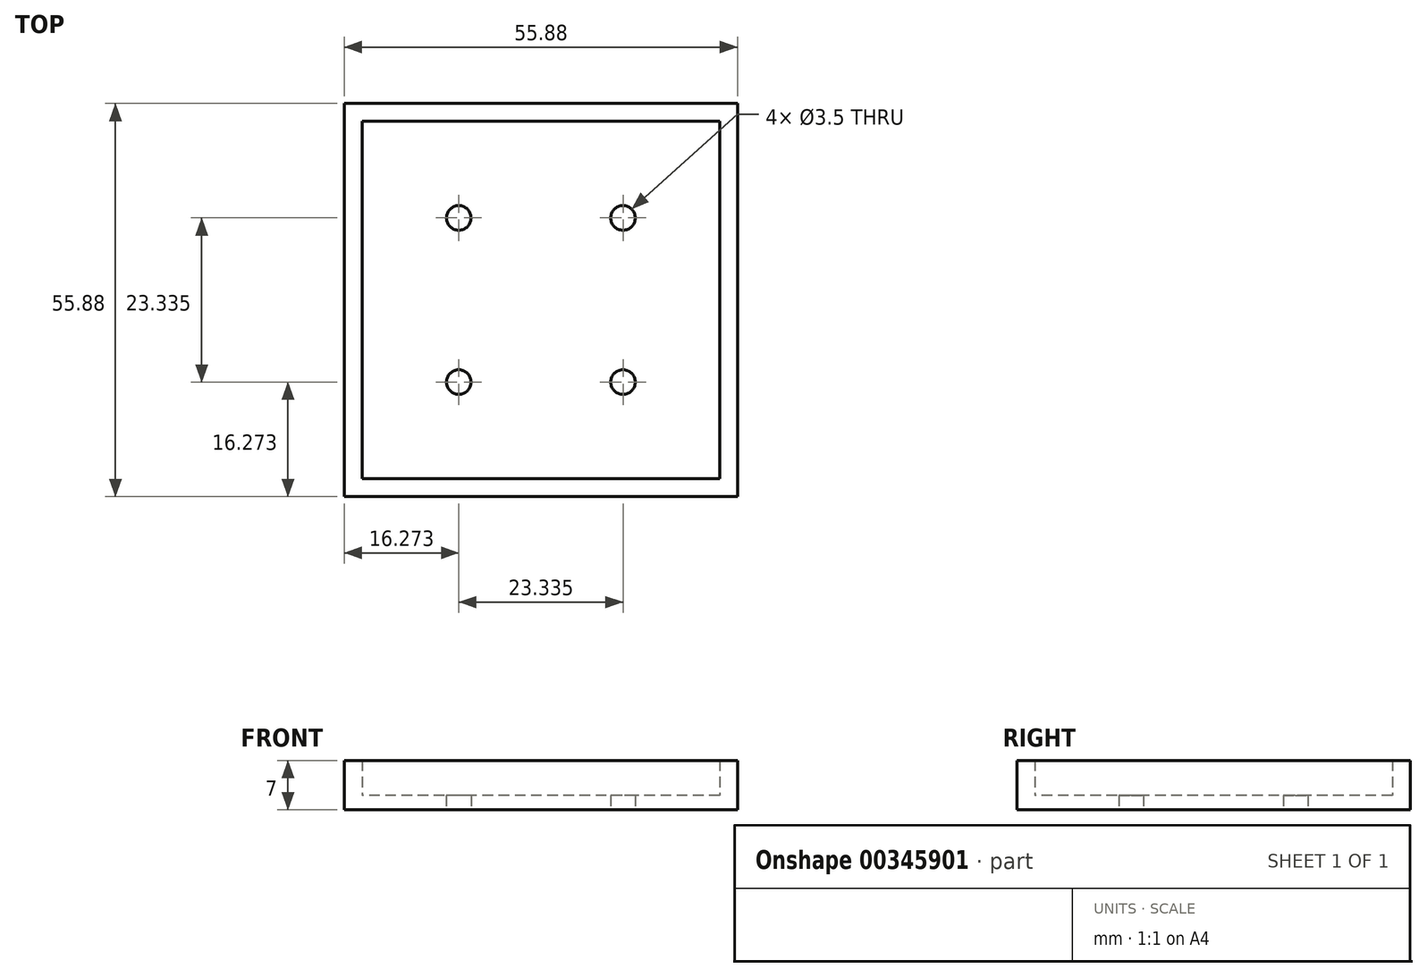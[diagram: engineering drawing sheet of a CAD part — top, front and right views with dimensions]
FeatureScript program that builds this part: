
annotation { "Feature Type Name" : "Feature", "Feature Type Description" : "" }
export const myFeature = defineFeature(function(context is Context, id is Id, definition is map)
    precondition{}
    {
        {
            var Q0;
            Q0=qCreatedBy(makeId("Top.planeOp"),FACE);
            var sketch = newSketch(context, id + "F0", { "sketchPlane" : qUnion([Q0])});
            skCircle(sketch, "E0", {"center": v(0, 0) * mm, "radius": 16.5 * mm, "construction": true});
            skCircle(sketch, "E1", {"center": v(-11.67, -11.67) * mm, "radius": 1.75 * mm});
            skCircle(sketch, "E2", {"center": v(-11.67, 11.67) * mm, "radius": 1.75 * mm});
            skCircle(sketch, "E3", {"center": v(11.67, 11.67) * mm, "radius": 1.75 * mm});
            skCircle(sketch, "E4", {"center": v(11.67, -11.67) * mm, "radius": 1.75 * mm});
            skLineSegment(sketch, "E5", {"start": v(-11.67, -11.67) * mm, "end": v(11.67, 11.67) * mm, "construction": true});
            skLineSegment(sketch, "E6", {"start": v(-11.67, 11.67) * mm, "end": v(11.67, -11.67) * mm, "construction": true});
            skLineSegment(sketch, "E7", {"start": v(-16.5, 0) * mm, "end": v(16.5, 0) * mm, "construction": true});
            skLineSegment(sketch, "E8.bottom", {"start": v(-27.94, 27.94) * mm, "end": v(27.94, 27.94) * mm});
            skLineSegment(sketch, "E8.top", {"start": v(-27.94, -27.94) * mm, "end": v(27.94, -27.94) * mm});
            skLineSegment(sketch, "E8.left", {"start": v(-27.94, 27.94) * mm, "end": v(-27.94, -27.94) * mm});
            skLineSegment(sketch, "E8.right", {"start": v(27.94, 27.94) * mm, "end": v(27.94, -27.94) * mm});
            skLineSegment(sketch, "E9", {"start": v(-27.94, -27.94) * mm, "end": v(27.94, 27.94) * mm, "construction": true});
            skSolve(sketch);
        }
        {
            var Q0;
            Q0=makeQuery(id+"F0.imprint","IMPRINT",FACE,{"disambiguationData":[TD([[makeQuery(id+"F0.imprint","IMPRINT",EDGE,{"derivedFrom":sQuery(id+"F0.wireOp",EDGE,"E1")}),-1.0]])]});
            extrude(context, id + "F1", {"entities" : qUnion([Q0]), "depth" : 2 * mm});
        }
        {
            var Q0;
            Q0=makeQuery(id+"F1.opExtrude","CAP_FACE",FACE,{"disambiguationData":[OSD([sQuery(id+"F0.wireOp",EDGE,"E1"),sQuery(id+"F0.wireOp",EDGE,"E2"),sQuery(id+"F0.wireOp",EDGE,"E3"),sQuery(id+"F0.wireOp",EDGE,"E4"),sQuery(id+"F0.wireOp",EDGE,"E8.bottom"),sQuery(id+"F0.wireOp",EDGE,"E8.top"),sQuery(id+"F0.wireOp",EDGE,"E8.left"),sQuery(id+"F0.wireOp",EDGE,"E8.right")])],"isStart":false});
            var sketch = newSketch(context, id + "F2", { "sketchPlane" : qUnion([Q0])});
            skLineSegment(sketch, "E10.bottom", {"start": v(-27.94, -27.94) * mm, "end": v(27.94, -27.94) * mm});
            skLineSegment(sketch, "E10.top", {"start": v(-27.94, 27.94) * mm, "end": v(27.94, 27.94) * mm});
            skLineSegment(sketch, "E10.left", {"start": v(-27.94, -27.94) * mm, "end": v(-27.94, 27.94) * mm});
            skLineSegment(sketch, "E10.right", {"start": v(27.94, -27.94) * mm, "end": v(27.94, 27.94) * mm});
            skLineSegment(sketch, "E11.bottom", {"start": v(25.4, 25.4) * mm, "end": v(-25.4, 25.4) * mm});
            skLineSegment(sketch, "E11.top", {"start": v(25.4, -25.4) * mm, "end": v(-25.4, -25.4) * mm});
            skLineSegment(sketch, "E11.left", {"start": v(25.4, 25.4) * mm, "end": v(25.4, -25.4) * mm});
            skLineSegment(sketch, "E11.right", {"start": v(-25.4, 25.4) * mm, "end": v(-25.4, -25.4) * mm});
            skSolve(sketch);
        }
        {
            var Q0;
            Q0=makeQuery(id+"F2.imprint","IMPRINT",FACE,{"disambiguationData":[TD([[makeQuery(id+"F2.imprint","IMPRINT",EDGE,{"derivedFrom":sQuery(id+"F2.wireOp",EDGE,"E10.bottom")}),1.0]])]});
            extrude(context, id + "F3", {"entities" : qUnion([Q0]), "operationType" : NewBodyOperationType.ADD, "depth" : 5 * mm});
        }
    });
